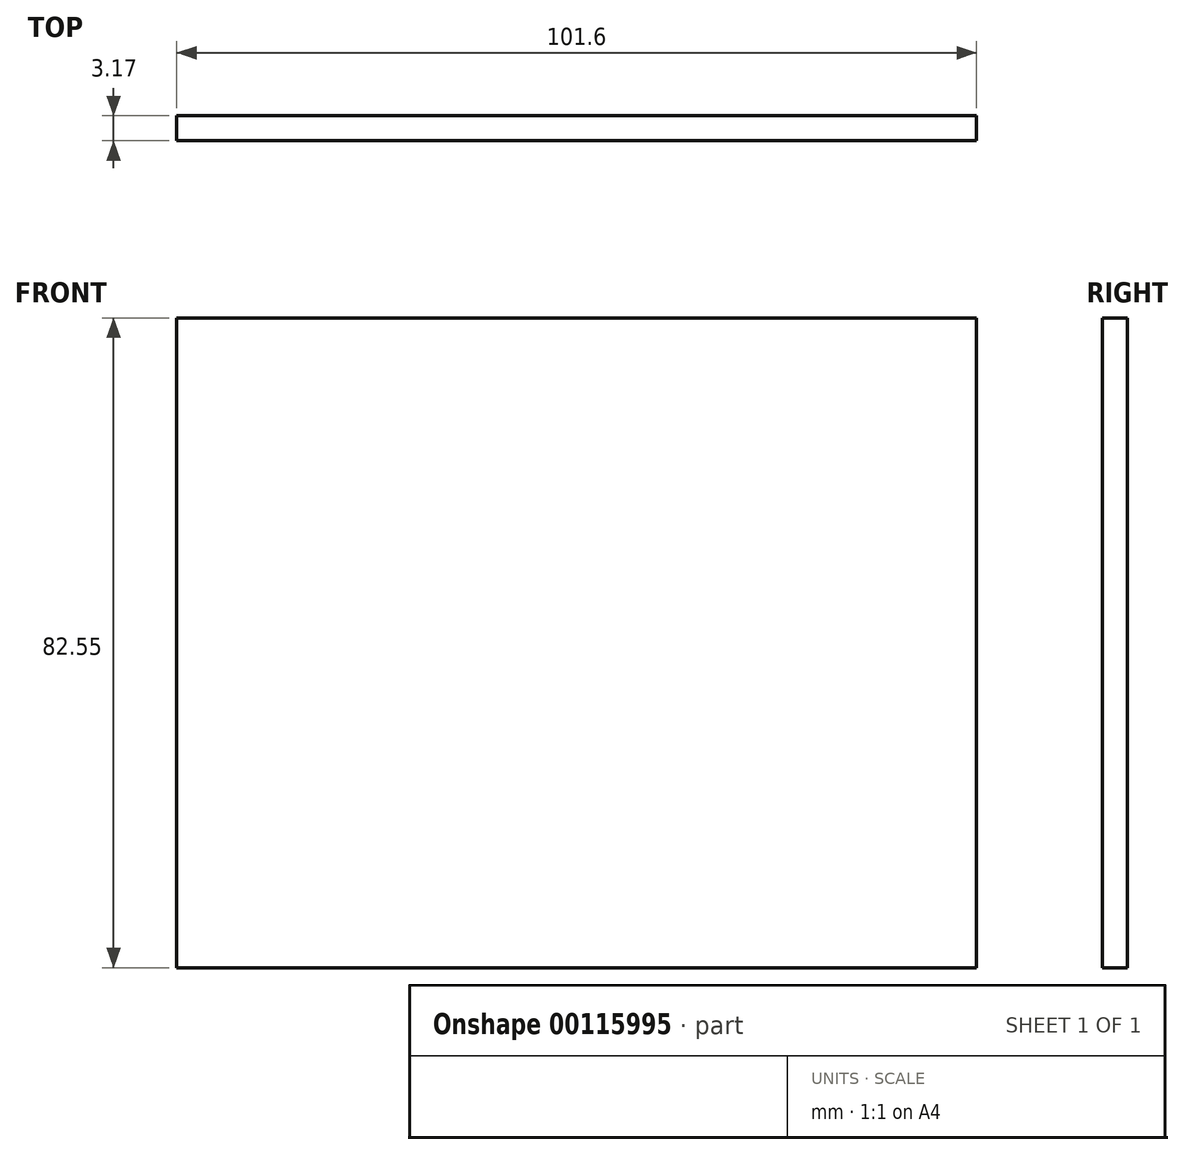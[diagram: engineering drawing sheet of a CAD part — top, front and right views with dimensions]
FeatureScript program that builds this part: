
annotation { "Feature Type Name" : "Feature", "Feature Type Description" : "" }
export const myFeature = defineFeature(function(context is Context, id is Id, definition is map)
    precondition{}
    {
        {
            var Q0;
            Q0=qCreatedBy(makeId("Front.planeOp"),FACE);
            var sketch = newSketch(context, id + "F0", { "sketchPlane" : qUnion([Q0])});
            skLineSegment(sketch, "E0.bottom", {"start": v(0, 0) * mm, "end": v(-101.6, 0) * mm});
            skLineSegment(sketch, "E0.top", {"start": v(0, 82.55) * mm, "end": v(-101.6, 82.55) * mm});
            skLineSegment(sketch, "E0.left", {"start": v(0, 0) * mm, "end": v(0, 82.55) * mm});
            skLineSegment(sketch, "E0.right", {"start": v(-101.6, 0) * mm, "end": v(-101.6, 82.55) * mm});
            skSolve(sketch);
        }
        {
            var Q0;
            Q0=makeQuery(id+"F0.imprint","IMPRINT",FACE,{"disambiguationData":[TD([[makeQuery(id+"F0.imprint","IMPRINT",EDGE,{"derivedFrom":sQuery(id+"F0.wireOp",EDGE,"E0.bottom")}),-1.0]])]});
            extrude(context, id + "F1", {"entities" : qUnion([Q0]), "depth" : 3.17 * mm});
        }
    });
